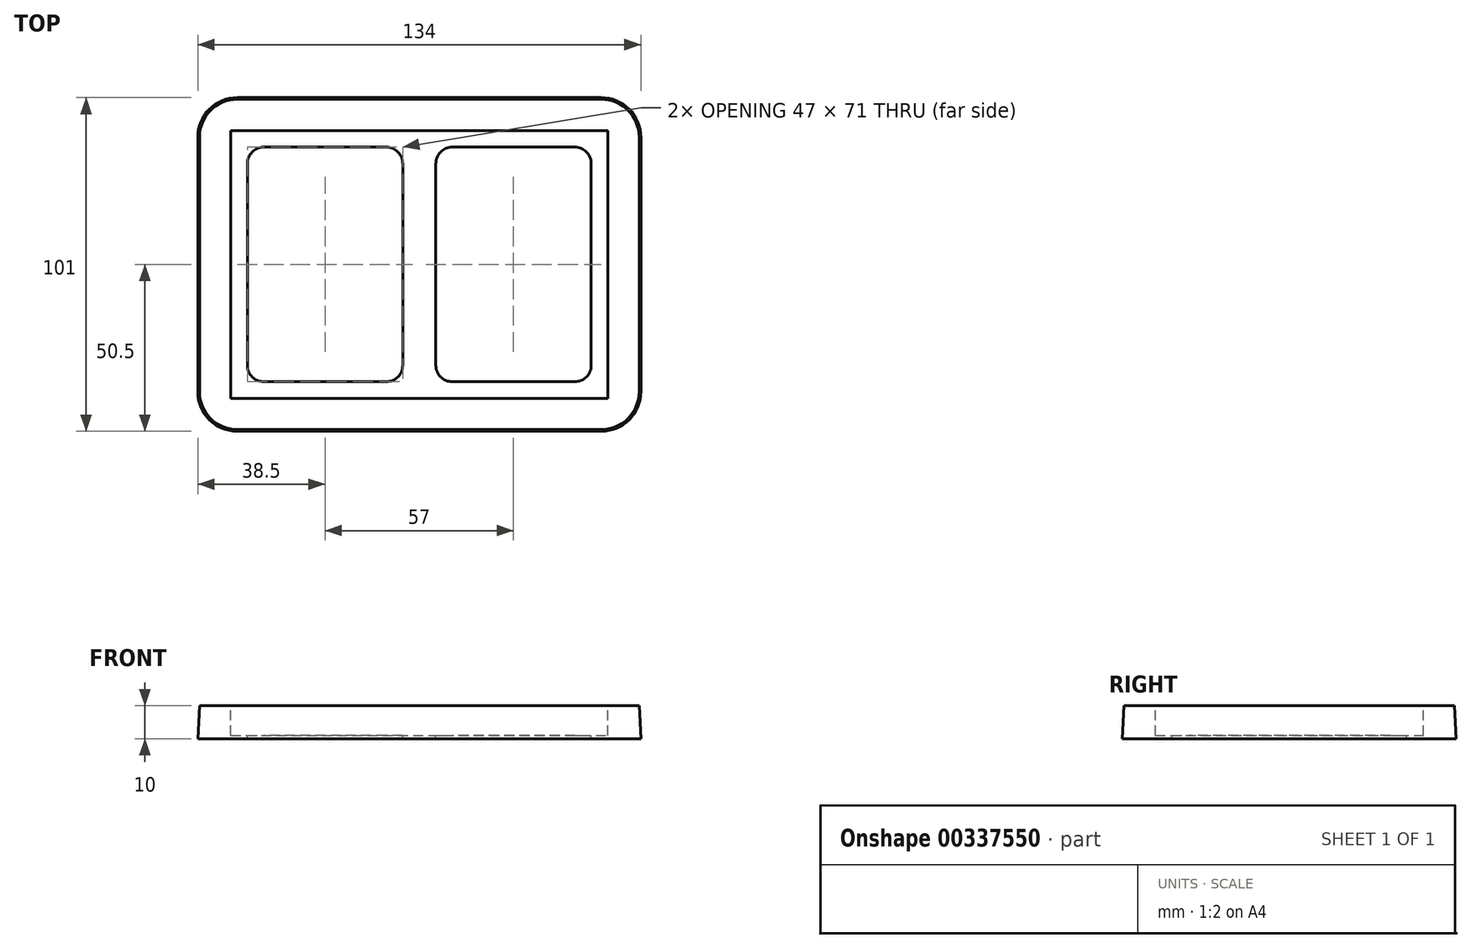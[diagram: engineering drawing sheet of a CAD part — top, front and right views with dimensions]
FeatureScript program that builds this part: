
annotation { "Feature Type Name" : "Feature", "Feature Type Description" : "" }
export const myFeature = defineFeature(function(context is Context, id is Id, definition is map)
    precondition{}
    {
        {
            var Q0;
            Q0=qCreatedBy(makeId("Top.planeOp"),FACE);
            var sketch = newSketch(context, id + "F0", { "sketchPlane" : qUnion([Q0])});
            skArc(sketch, "E0.0", {"start": v(-55, 50.5) * mm, "mid": v(-63.49, 46.99) * mm, "end": v(-67, 38.5) * mm});
            skLineSegment(sketch, "E0.1", {"start": v(-67, 38.5) * mm, "end": v(-67, -38.5) * mm});
            skLineSegment(sketch, "E0.2", {"start": v(-55, 50.5) * mm, "end": v(55, 50.5) * mm});
            skArc(sketch, "E0.3", {"start": v(-67, -38.5) * mm, "mid": v(-63.49, -46.99) * mm, "end": v(-55, -50.5) * mm});
            skArc(sketch, "E0.4", {"start": v(67, 38.5) * mm, "mid": v(63.49, 46.99) * mm, "end": v(55, 50.5) * mm});
            skLineSegment(sketch, "E0.5", {"start": v(67, 38.5) * mm, "end": v(67, -38.5) * mm});
            skArc(sketch, "E0.6", {"start": v(55, -50.5) * mm, "mid": v(63.49, -46.99) * mm, "end": v(67, -38.5) * mm});
            skLineSegment(sketch, "E0.7", {"start": v(-55, -50.5) * mm, "end": v(55, -50.5) * mm});
            skSolve(sketch);
        }
        {
            var Q0;
            Q0=makeQuery(id+"F0.imprint","IMPRINT",FACE,{"disambiguationData":[TD([[makeQuery(id+"F0.imprint","IMPRINT",EDGE,{"derivedFrom":sQuery(id+"F0.wireOp",EDGE,"E0.0")}),1.0]])]});
            extrude(context, id + "F1", {"entities" : qUnion([Q0]), "depth" : 10 * mm, "hasDraft" : true, "draftAngle" : 3 * degree, "draftPullDirection" : true});
        }
        {
            var Q0;
            Q0=makeQuery(id+"F1.opExtrude","CAP_FACE",FACE,{"disambiguationData":[OSD([sQuery(id+"F0.wireOp",EDGE,"E0.0"),sQuery(id+"F0.wireOp",EDGE,"E0.1"),sQuery(id+"F0.wireOp",EDGE,"E0.2"),sQuery(id+"F0.wireOp",EDGE,"E0.3"),sQuery(id+"F0.wireOp",EDGE,"E0.4"),sQuery(id+"F0.wireOp",EDGE,"E0.5"),sQuery(id+"F0.wireOp",EDGE,"E0.6"),sQuery(id+"F0.wireOp",EDGE,"E0.7")])],"isStart":false});
            var sketch = newSketch(context, id + "F2", { "sketchPlane" : qUnion([Q0])});
            skLineSegment(sketch, "E1.bottom", {"start": v(-57, -40.5) * mm, "end": v(57, -40.5) * mm});
            skLineSegment(sketch, "E1.top", {"start": v(-57, 40.5) * mm, "end": v(57, 40.5) * mm});
            skLineSegment(sketch, "E1.left", {"start": v(-57, -40.5) * mm, "end": v(-57, 40.5) * mm});
            skLineSegment(sketch, "E1.right", {"start": v(57, -40.5) * mm, "end": v(57, 40.5) * mm});
            skPoint(sketch, "E1.middle", {"position": v(0, 0) * mm});
            skSolve(sketch);
        }
        {
            var Q0;
            Q0 = qSketchRegion(id + "F2", true);
            extrude(context, id + "F3", {"entities" : qUnion([Q0]), "operationType" : NewBodyOperationType.REMOVE, "oppositeDirection" : true, "depth" : 9 * mm});
        }
        {
            var Q0;
            Q0=makeQuery(id+"F3.boolean.opBoolean","COPY",FACE,{"derivedFrom":makeQuery(id+"F3.opExtrude","CAP_FACE",FACE,{"disambiguationData":[OSD([sQuery(id+"F2.wireOp",EDGE,"E1.bottom"),sQuery(id+"F2.wireOp",EDGE,"E1.top"),sQuery(id+"F2.wireOp",EDGE,"E1.left"),sQuery(id+"F2.wireOp",EDGE,"E1.right")])],"isStart":false})});
            var sketch = newSketch(context, id + "F4", { "sketchPlane" : qUnion([Q0])});
            skLineSegment(sketch, "E2.bottom", {"start": v(47, 35.5) * mm, "end": v(10, 35.5) * mm});
            skLineSegment(sketch, "E2.top", {"start": v(47, -35.5) * mm, "end": v(10, -35.5) * mm});
            skLineSegment(sketch, "E2.left", {"start": v(52, 30.5) * mm, "end": v(52, -30.5) * mm});
            skLineSegment(sketch, "E2.right", {"start": v(5, 30.5) * mm, "end": v(5, -30.5) * mm});
            skPoint(sketch, "E3.visualSharp", {"position": v(52, 35.5) * mm});
            skArc(sketch, "E3.filletArc", {"start": v(52, 30.5) * mm, "mid": v(50.54, 34.04) * mm, "end": v(47, 35.5) * mm});
            skPoint(sketch, "E4.visualSharp", {"position": v(52, -35.5) * mm});
            skArc(sketch, "E4.filletArc", {"start": v(47, -35.5) * mm, "mid": v(50.54, -34.04) * mm, "end": v(52, -30.5) * mm});
            skPoint(sketch, "E5.visualSharp", {"position": v(5, -35.5) * mm});
            skArc(sketch, "E5.filletArc", {"start": v(5, -30.5) * mm, "mid": v(6.46, -34.04) * mm, "end": v(10, -35.5) * mm});
            skPoint(sketch, "E6.visualSharp", {"position": v(5, 35.5) * mm});
            skArc(sketch, "E6.filletArc", {"start": v(10, 35.5) * mm, "mid": v(6.46, 34.04) * mm, "end": v(5, 30.5) * mm});
            skLineSegment(sketch, "E7.1.0.0", {"start": v(-5, 30.5) * mm, "end": v(-5, -30.5) * mm});
            skArc(sketch, "E7.1.0.1", {"start": v(-10, -35.5) * mm, "mid": v(-6.46, -34.04) * mm, "end": v(-5, -30.5) * mm});
            skLineSegment(sketch, "E7.1.0.2", {"start": v(-10, -35.5) * mm, "end": v(-47, -35.5) * mm});
            skArc(sketch, "E7.1.0.3", {"start": v(-52, -30.5) * mm, "mid": v(-50.54, -34.04) * mm, "end": v(-47, -35.5) * mm});
            skLineSegment(sketch, "E7.1.0.4", {"start": v(-52, 30.5) * mm, "end": v(-52, -30.5) * mm});
            skArc(sketch, "E7.1.0.5", {"start": v(-47, 35.5) * mm, "mid": v(-50.54, 34.04) * mm, "end": v(-52, 30.5) * mm});
            skLineSegment(sketch, "E7.1.0.6", {"start": v(-10, 35.5) * mm, "end": v(-47, 35.5) * mm});
            skArc(sketch, "E7.1.0.7", {"start": v(-5, 30.5) * mm, "mid": v(-6.46, 34.04) * mm, "end": v(-10, 35.5) * mm});
            skLineSegment(sketch, "E7.direction1", {"start": v(52, -30.5) * mm, "end": v(-5, -30.5) * mm, "construction": true});
            skSolve(sketch);
        }
        {
            var Q0;
            Q0 = qSketchRegion(id + "F4", true);
            extrude(context, id + "F5", {"entities" : qUnion([Q0]), "operationType" : NewBodyOperationType.REMOVE, "endBound" : BoundingType.UP_TO_NEXT, "oppositeDirection" : true, "depth" : 25 * mm});
        }
    });
